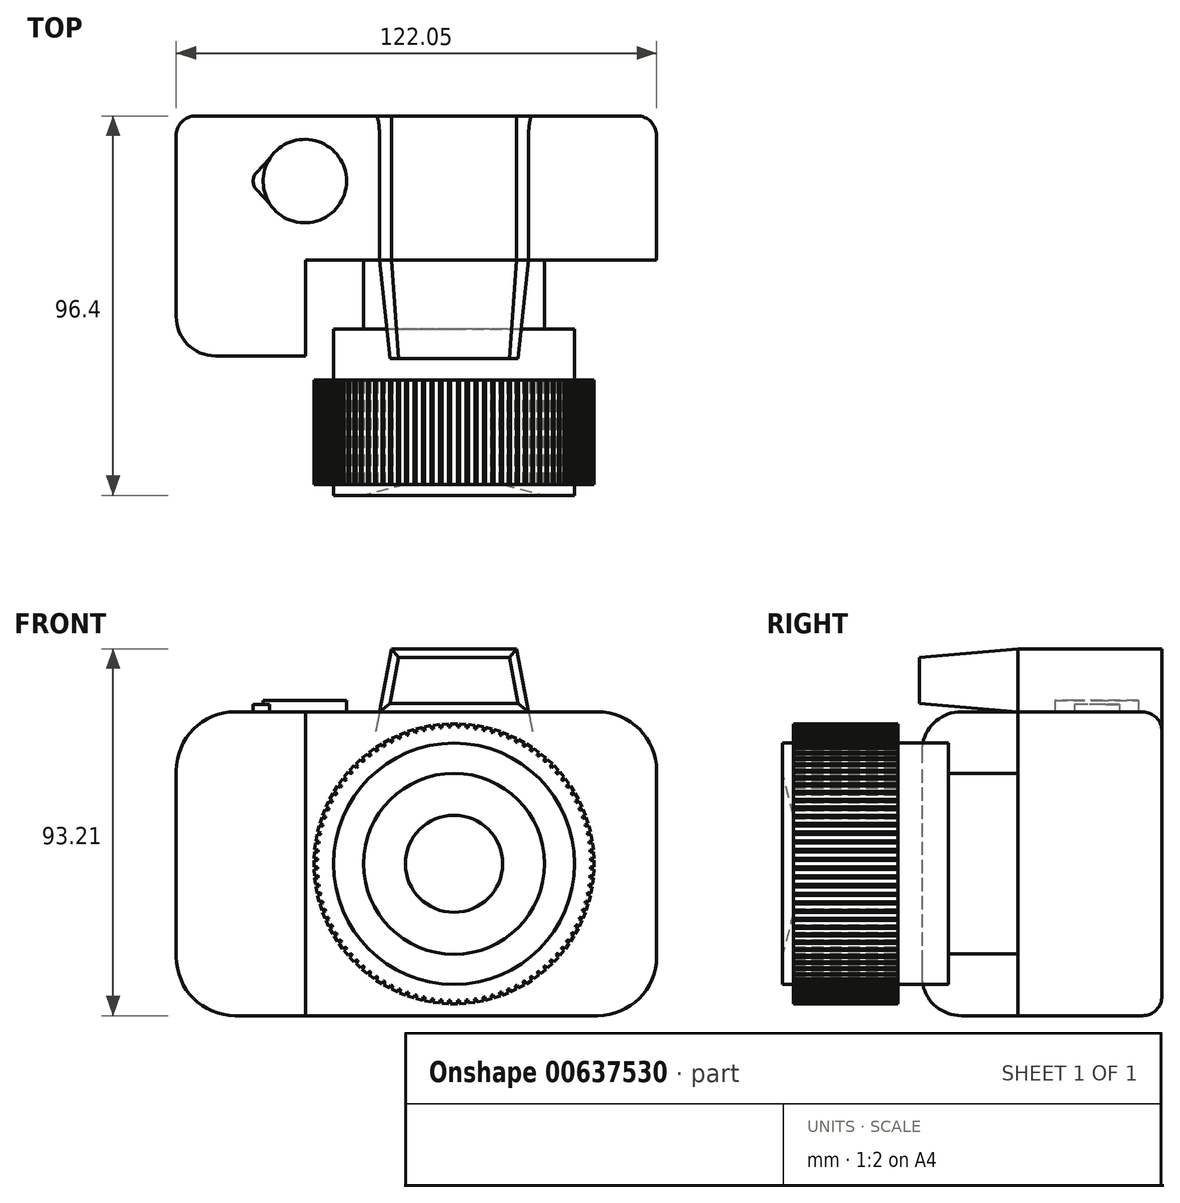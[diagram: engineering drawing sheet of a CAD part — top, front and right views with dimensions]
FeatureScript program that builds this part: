
annotation { "Feature Type Name" : "Feature", "Feature Type Description" : "" }
export const myFeature = defineFeature(function(context is Context, id is Id, definition is map)
    precondition{}
    {
        {
            var Q0;
            Q0=qCreatedBy(makeId("Front.planeOp"),FACE);
            var sketch = newSketch(context, id + "F0", { "sketchPlane" : qUnion([Q0])});
            skCircle(sketch, "E0", {"center": v(0, 0) * mm, "radius": 22.94 * mm});
            skCircle(sketch, "E1", {"center": v(0, 0) * mm, "radius": 26.37 * mm});
            skLineSegment(sketch, "E2", {"start": v(0, 54.62) * mm, "end": v(-15.9, 54.62) * mm});
            skLineSegment(sketch, "E3", {"start": v(-15.9, 54.62) * mm, "end": v(-24.34, 10.14) * mm});
            skLineSegment(sketch, "E4", {"start": v(-24.34, 10.14) * mm, "end": v(0, 10.14) * mm});
            skLineSegment(sketch, "E5.MirrorCS", {"start": v(0, 54.62) * mm, "end": v(15.9, 54.62) * mm});
            skLineSegment(sketch, "E6.MirrorCS", {"start": v(15.9, 54.62) * mm, "end": v(24.34, 10.14) * mm});
            skLineSegment(sketch, "E7.MirrorCS", {"start": v(24.34, 10.14) * mm, "end": v(0, 10.14) * mm});
            skCircle(sketch, "E8", {"center": v(0, 0) * mm, "radius": 34.73 * mm});
            skCircle(sketch, "E9", {"center": v(0, 0) * mm, "radius": 30.64 * mm});
            skSolve(sketch);
        }
        {
            var Q0;
            Q0=makeQuery(id+"F0.imprint","IMPRINT",FACE,{"disambiguationData":[TD([[makeQuery(id+"F0.imprint","IMPRINT",EDGE,{"derivedFrom":sQuery(id+"F0.wireOp",EDGE,"E0")}),1.0]])]});
            extrude(context, id + "F1", {"entities" : qUnion([Q0]), "depth" : 59.8 * mm, "offsetDistance" : 25 * mm});
        }
        {
            var Q0;
            Q0=makeQuery(id+"F0.imprint","IMPRINT",FACE,{"disambiguationData":[TD([[makeQuery(id+"F0.imprint","IMPRINT",EDGE,{"derivedFrom":sQuery(id+"F0.wireOp",EDGE,"E0")}),-1.0]])]});
            var Q1;
            {var subQ0=sQuery(id+"F0.wireOp",EDGE,"E3");var subQ5=sQuery(id+"F0.wireOp",EDGE,"E9");var subQ7=makeQuery(id+"F0.imprint","INTERSECT",VERTEX,{"derivedFrom":[subQ0,subQ5]});Q1=makeQuery(id+"F0.imprint","IMPRINT",FACE,{"disambiguationData":[TD([[makeQuery(id+"F0.imprint","IMPRINT",EDGE,{"disambiguationData":[TD([[subQ7,-1.0]])],"derivedFrom":subQ5}),1.0]])]});}
            var Q2;
            {var subQ0=sQuery(id+"F0.wireOp",EDGE,"E3");var subQ5=sQuery(id+"F0.wireOp",EDGE,"E9");var subQ6=makeQuery(id+"F0.imprint","INTERSECT",VERTEX,{"derivedFrom":[subQ0,subQ5]});Q2=makeQuery(id+"F0.imprint","IMPRINT",FACE,{"disambiguationData":[TD([[makeQuery(id+"F0.imprint","IMPRINT",EDGE,{"disambiguationData":[TD([[subQ6,1.0]])],"derivedFrom":subQ5}),1.0]])]});}
            var Q3;
            Q3=makeQuery(id+"F1.opExtrude","CAP_FACE",FACE,{"disambiguationData":[OSD([sQuery(id+"F0.wireOp",EDGE,"E0")])],"isStart":false});
            extrude(context, id + "F2", {"entities" : qUnion([Q0, Q1, Q2]), "operationType" : NewBodyOperationType.ADD, "endBound" : BoundingType.UP_TO_SURFACE, "depth" : 25 * mm, "endBoundEntityFace" : qUnion([Q3]), "offsetDistance" : 25 * mm, "hasSecondDirection" : true, "secondDirectionOppositeDirection" : false, "secondDirectionDepth" : 17.6 * mm});
        }
        {
            var Q0;
            Q0=qCreatedBy(makeId("Right.planeOp"),FACE);
            var sketch = newSketch(context, id + "F3", { "sketchPlane" : qUnion([Q0])});
            skLineSegment(sketch, "E10", {"start": v(-53.76, 0) * mm, "end": v(-60, -23.79) * mm});
            skLineSegment(sketch, "E11", {"start": v(-60, -23.79) * mm, "end": v(-60, 0) * mm});
            skLineSegment(sketch, "E12", {"start": v(-60, 0) * mm, "end": v(-53.76, 0) * mm});
            skSolve(sketch);
        }
        {
            var Q0;
            Q0=makeQuery(id+"F3.imprint","IMPRINT",FACE,{"disambiguationData":[TD([[makeQuery(id+"F3.imprint","IMPRINT",EDGE,{"derivedFrom":sQuery(id+"F3.wireOp",EDGE,"E10")}),-1.0]])]});
            var Q1;
            Q1=sQuery(id+"F3.wireOp",EDGE,"E12");
            revolve(context, id + "F4", {"operationType" : NewBodyOperationType.REMOVE, "entities" : qUnion([Q0]), "axis" : qUnion([Q1]), "revolveType" : RevolveType.FULL, "oppositeDirection" : true});
        }
        {
            var Q0;
            Q0=qCreatedBy(makeId("Front.planeOp"),FACE);
            var sketch = newSketch(context, id + "F5", { "sketchPlane" : qUnion([Q0])});
            skLineSegment(sketch, "E13.bottom", {"start": v(-55.59, 38.6) * mm, "end": v(36.46, 38.6) * mm});
            skPoint(sketch, "E14.visualSharp", {"position": v(51.46, 38.6) * mm});
            skArc(sketch, "E14.filletArc", {"start": v(51.46, 23.6) * mm, "mid": v(47.06, 34.2) * mm, "end": v(36.46, 38.6) * mm});
            skPoint(sketch, "E15.visualSharp", {"position": v(51.46, -43.73) * mm});
            skPoint(sketch, "E16.visualSharp", {"position": v(-70.59, 38.6) * mm});
            skArc(sketch, "E16.filletArc", {"start": v(-55.59, 38.6) * mm, "mid": v(-66.2, 34.2) * mm, "end": v(-70.59, 23.6) * mm});
            skPoint(sketch, "E17.visualSharp", {"position": v(-70.59, -43.73) * mm});
            skLineSegment(sketch, "E18.MirrorCS", {"start": v(-55.59, -38.6) * mm, "end": v(36.46, -38.6) * mm});
            skArc(sketch, "E19.MirrorCS", {"start": v(-55.59, -38.6) * mm, "mid": v(-66.2, -34.2) * mm, "end": v(-70.59, -23.6) * mm});
            skArc(sketch, "E20.MirrorCS", {"start": v(51.46, -23.6) * mm, "mid": v(47.06, -34.2) * mm, "end": v(36.46, -38.6) * mm});
            skLineSegment(sketch, "E21", {"start": v(51.46, 23.6) * mm, "end": v(51.46, -23.6) * mm});
            skLineSegment(sketch, "E22", {"start": v(-70.59, 23.6) * mm, "end": v(-70.59, -23.6) * mm});
            skLineSegment(sketch, "E23.0", {"start": v(-15.9, 54.62) * mm, "end": v(-24.34, 10.14) * mm});
            skLineSegment(sketch, "E24.0", {"start": v(15.9, 54.62) * mm, "end": v(24.34, 10.14) * mm});
            skLineSegment(sketch, "E25", {"start": v(18.94, 38.6) * mm, "end": v(-18.94, 38.6) * mm});
            skLineSegment(sketch, "E26", {"start": v(-18.94, 38.6) * mm, "end": v(-15.9, 54.62) * mm});
            skLineSegment(sketch, "E27", {"start": v(15.9, 54.62) * mm, "end": v(18.94, 38.6) * mm});
            skLineSegment(sketch, "E28", {"start": v(15.9, 54.62) * mm, "end": v(-15.9, 54.62) * mm});
            skSolve(sketch);
        }
        {
            var Q0;
            Q0=makeQuery(id+"F5.imprint","IMPRINT",FACE,{"disambiguationData":[TD([[makeQuery(id+"F5.imprint","IMPRINT",EDGE,{"derivedFrom":sQuery(id+"F5.wireOp",EDGE,"E13.bottom")}),-1.0]])]});
            var Q1;
            {var subQ4=sQuery(id+"F0.wireOp",EDGE,"E2");Q1=makeQuery(id+"F0.imprint","IMPRINT",FACE,{"disambiguationData":[TD([[makeQuery(id+"F0.imprint","IMPRINT",EDGE,{"derivedFrom":subQ4}),1.0]])]});}
            var Q2;
            {var subQ4=sQuery(id+"F0.wireOp",EDGE,"E5.MirrorCS");Q2=makeQuery(id+"F0.imprint","IMPRINT",FACE,{"disambiguationData":[TD([[makeQuery(id+"F0.imprint","IMPRINT",EDGE,{"derivedFrom":subQ4}),-1.0]])]});}
            extrude(context, id + "F6", {"entities" : qUnion([Q0, Q1, Q2]), "operationType" : NewBodyOperationType.ADD, "oppositeDirection" : true, "depth" : 36.6 * mm, "offsetDistance" : 25 * mm});
        }
        {
            var Q0;
            Q0=qCreatedBy(makeId("Front.planeOp"),FACE);
            var sketch = newSketch(context, id + "F7", { "sketchPlane" : qUnion([Q0])});
            skLineSegment(sketch, "E29.0", {"start": v(0, 54.62) * mm, "end": v(-15.9, 54.62) * mm});
            skLineSegment(sketch, "E30.0", {"start": v(0, 54.62) * mm, "end": v(15.9, 54.62) * mm});
            skLineSegment(sketch, "E31.0", {"start": v(-15.9, 54.62) * mm, "end": v(-24.34, 10.14) * mm});
            skLineSegment(sketch, "E32.0", {"start": v(15.9, 54.62) * mm, "end": v(24.34, 10.14) * mm});
            skLineSegment(sketch, "E33.0", {"start": v(-55.59, 38.6) * mm, "end": v(-18.94, 38.6) * mm});
            skLineSegment(sketch, "E34", {"start": v(-18.94, 38.6) * mm, "end": v(18.94, 38.6) * mm});
            skLineSegment(sketch, "E35", {"start": v(18.94, 38.6) * mm, "end": v(15.9, 54.62) * mm});
            skLineSegment(sketch, "E36", {"start": v(-15.9, 54.62) * mm, "end": v(15.9, 54.62) * mm});
            skSolve(sketch);
        }
        {
            var Q0;
            {var subQ2=sQuery(id+"F7.wireOp",EDGE,"E34");Q0=makeQuery(id+"F7.imprint","IMPRINT",FACE,{"disambiguationData":[TD([[makeQuery(id+"F7.imprint","IMPRINT",EDGE,{"derivedFrom":subQ2}),1.0]])]});}
            extrude(context, id + "F8", {"entities" : qUnion([Q0]), "operationType" : NewBodyOperationType.ADD, "depth" : 25 * mm, "offsetDistance" : 25 * mm, "hasDraft" : true, "draftAngle" : 5 * degree, "draftPullDirection" : true});
        }
        {
            var Q0;
            Q0=qCreatedBy(makeId("Top.planeOp"),FACE);
            var sketch = newSketch(context, id + "F9", { "sketchPlane" : qUnion([Q0])});
            skLineSegment(sketch, "E37.0", {"start": v(-55.59, 0) * mm, "end": v(-70.59, 0) * mm});
            skLineSegment(sketch, "E38", {"start": v(-70.59, 0) * mm, "end": v(-37.71, 0) * mm});
            skLineSegment(sketch, "E39", {"start": v(-37.71, 0) * mm, "end": v(-37.71, -24.4) * mm});
            skLineSegment(sketch, "E40", {"start": v(-37.71, -24.4) * mm, "end": v(-70.59, -24.4) * mm});
            skLineSegment(sketch, "E41", {"start": v(-70.59, -24.4) * mm, "end": v(-70.59, 0) * mm});
            skSolve(sketch);
        }
        {
            var Q0;
            {var subQ2=sQuery(id+"F9.wireOp",EDGE,"E39");Q0=makeQuery(id+"F9.imprint","IMPRINT",FACE,{"disambiguationData":[TD([[makeQuery(id+"F9.imprint","IMPRINT",EDGE,{"derivedFrom":subQ2}),-1.0]])]});}
            var Q1;
            {var subQ0=sQuery(id+"F0.wireOp",EDGE,"E3");var subQ5=sQuery(id+"F5.wireOp",EDGE,"E25");var subQ13=sQuery(id+"F5.wireOp",EDGE,"E13.bottom");Q1=makeQuery(id+"F6.boolean.opBoolean","SPLIT",FACE,{"disambiguationData":[TD([makeQuery(id+"F6.opExtrude","SWEPT_FACE",FACE,{"disambiguationData":[OSD([subQ0])]})])],"derivedFrom":makeQuery(id+"F6.opExtrude","SWEPT_FACE",FACE,{"disambiguationData":[OSD([subQ13,subQ5])]})});}
            var Q2;
            Q2=makeQuery(id+"F6.opExtrude","SWEPT_FACE",FACE,{"disambiguationData":[OSD([sQuery(id+"F5.wireOp",EDGE,"E18.MirrorCS")])]});
            extrude(context, id + "F10", {"entities" : qUnion([Q0]), "operationType" : NewBodyOperationType.ADD, "endBound" : BoundingType.UP_TO_SURFACE, "depth" : 25 * mm, "endBoundEntityFace" : qUnion([Q1]), "offsetDistance" : 25 * mm, "hasSecondDirection" : true, "secondDirectionBound" : SecondDirectionBoundingType.UP_TO_SURFACE, "secondDirectionOppositeDirection" : true, "secondDirectionDepth" : 25 * mm, "secondDirectionBoundEntityFace" : qUnion([Q2])});
        }
        {
            var Q0;
            Q0=makeQuery(id+"F10.opExtrude","CAP_EDGE",EDGE,{"disambiguationData":[OSD([sQuery(id+"F9.wireOp",EDGE,"E41")])],"isStart":false});
            var Q1;
            Q1=makeQuery(id+"F10.opExtrude","CAP_EDGE",EDGE,{"disambiguationData":[OSD([sQuery(id+"F9.wireOp",EDGE,"E41")])],"isStart":true});
            fillet(context, id + "F11", {"entities" : qUnion([Q0, Q1]), "radius" : 15 * mm, "tangentPropagation" : true, "allowEdgeOverflow" : false});
        }
        {
            var Q0;
            Q0=makeQuery(id+"F10.opExtrude","TWEAK_EDGE",EDGE,{"derivedFrom":[makeQuery(id+"F9.imprint","IMPRINT",EDGE,{"derivedFrom":sQuery(id+"F9.wireOp",EDGE,"E39")}),makeQuery(id+"F9.imprint","IMPRINT",EDGE,{"derivedFrom":sQuery(id+"F9.wireOp",EDGE,"E40")})]});
            var Q1;
            Q1=makeQuery(id+"F10.opExtrude","CAP_EDGE",EDGE,{"disambiguationData":[OSD([sQuery(id+"F9.wireOp",EDGE,"E40")])],"isStart":false});
            fillet(context, id + "F12", {"entities" : qUnion([Q0, Q1]), "radius" : 10 * mm, "tangentPropagation" : true, "allowEdgeOverflow" : false});
        }
        {
            var Q0;
            {var subQ0=sQuery(id+"F0.wireOp",EDGE,"E3");var subQ1=sQuery(id+"F5.wireOp",EDGE,"E25");var subQ9=sQuery(id+"F5.wireOp",EDGE,"E13.bottom");Q0=makeQuery(id+"F10.boolean.opBoolean","MERGE",FACE,{"derivedFrom":[makeQuery(id+"F6.boolean.opBoolean","SPLIT",FACE,{"disambiguationData":[TD([makeQuery(id+"F6.opExtrude","SWEPT_FACE",FACE,{"disambiguationData":[OSD([subQ0])]})])],"derivedFrom":makeQuery(id+"F6.opExtrude","SWEPT_FACE",FACE,{"disambiguationData":[OSD([subQ9,subQ1])]})}),makeQuery(id+"F10.opExtrude","CAP_FACE",FACE,{"disambiguationData":[OSD([sQuery(id+"F9.wireOp",EDGE,"E38"),sQuery(id+"F9.wireOp",EDGE,"E39"),sQuery(id+"F9.wireOp",EDGE,"E40"),sQuery(id+"F9.wireOp",EDGE,"E41")])],"isStart":false})]});}
            var sketch = newSketch(context, id + "F13", { "sketchPlane" : qUnion([Q0])});
            skCircle(sketch, "E42", {"center": v(-37.91, 20.04) * mm, "radius": 10.6 * mm});
            skLineSegment(sketch, "E43", {"start": v(-52.33, 20.04) * mm, "end": v(-46.82, 25.77) * mm});
            skLineSegment(sketch, "E44", {"start": v(-52.33, 20.04) * mm, "end": v(-37.91, 20.04) * mm});
            skLineSegment(sketch, "E45.MirrorCS", {"start": v(-52.33, 20.04) * mm, "end": v(-46.82, 14.3) * mm});
            skSolve(sketch);
        }
        {
            var Q0;
            Q0=makeQuery(id+"F13.imprint","IMPRINT",FACE,{"disambiguationData":[TD([[makeQuery(id+"F13.imprint","IMPRINT",EDGE,{"derivedFrom":sQuery(id+"F13.wireOp",EDGE,"E42")}),1.0]])]});
            extrude(context, id + "F14", {"entities" : qUnion([Q0]), "operationType" : NewBodyOperationType.ADD, "depth" : 2.9 * mm, "offsetDistance" : 25 * mm});
        }
        {
            var Q0;
            {var subQ0=sQuery(id+"F0.wireOp",EDGE,"E3");var subQ5=sQuery(id+"F0.wireOp",EDGE,"E8");var subQ6=makeQuery(id+"F0.imprint","INTERSECT",VERTEX,{"derivedFrom":[subQ0,subQ5]});Q0=makeQuery(id+"F0.imprint","IMPRINT",FACE,{"disambiguationData":[TD([[makeQuery(id+"F0.imprint","IMPRINT",EDGE,{"disambiguationData":[TD([[subQ6,-1.0]])],"derivedFrom":subQ5}),1.0]])]});}
            var Q1;
            {var subQ0=sQuery(id+"F0.wireOp",EDGE,"E3");var subQ5=sQuery(id+"F0.wireOp",EDGE,"E8");var subQ6=makeQuery(id+"F0.imprint","INTERSECT",VERTEX,{"derivedFrom":[subQ0,subQ5]});Q1=makeQuery(id+"F0.imprint","IMPRINT",FACE,{"disambiguationData":[TD([[makeQuery(id+"F0.imprint","IMPRINT",EDGE,{"disambiguationData":[TD([[subQ6,1.0]])],"derivedFrom":subQ5}),1.0]])]});}
            var Q2;
            {var subQ0=sQuery(id+"F0.wireOp",EDGE,"E0");Q2=makeQuery(id+"F2.boolean.opBoolean","MERGE",FACE,{"derivedFrom":[makeQuery(id+"F1.opExtrude","CAP_FACE",FACE,{"disambiguationData":[OSD([subQ0])],"isStart":false}),makeQuery(id+"F2.opExtrude","CAP_FACE",FACE,{"disambiguationData":[OSD([subQ0,sQuery(id+"F0.wireOp",EDGE,"E9")])],"isStart":false})]});}
            extrude(context, id + "F15", {"entities" : qUnion([Q0, Q1]), "operationType" : NewBodyOperationType.ADD, "depth" : 57 * mm, "endBoundEntityFace" : qUnion([Q2]), "offsetDistance" : 25 * mm, "hasSecondDirection" : true, "secondDirectionOppositeDirection" : false, "secondDirectionDepth" : 30.5 * mm});
        }
        {
            var Q0;
            {var subQ0=sQuery(id+"F13.wireOp",EDGE,"E43");Q0=makeQuery(id+"F13.imprint","IMPRINT",FACE,{"disambiguationData":[TD([[makeQuery(id+"F13.imprint","IMPRINT",EDGE,{"derivedFrom":subQ0}),-1.0]])]});}
            var Q1;
            {var subQ0=sQuery(id+"F13.wireOp",EDGE,"E45.MirrorCS");Q1=makeQuery(id+"F13.imprint","IMPRINT",FACE,{"disambiguationData":[TD([[makeQuery(id+"F13.imprint","IMPRINT",EDGE,{"derivedFrom":subQ0}),1.0]])]});}
            extrude(context, id + "F16", {"entities" : qUnion([Q0, Q1]), "operationType" : NewBodyOperationType.ADD, "depth" : 1.83 * mm, "offsetDistance" : 25 * mm});
        }
        {
            var Q0;
            Q0=makeQuery(id+"F16.opExtrude","SWEPT_EDGE",EDGE,{"disambiguationData":[OSD([sQuery(id+"F13.wireOp",EDGE,"E43"),sQuery(id+"F13.wireOp",EDGE,"E44"),sQuery(id+"F13.wireOp",EDGE,"E45.MirrorCS")])]});
            fillet(context, id + "F17", {"entities" : qUnion([Q0]), "radius" : 3.36 * mm, "tangentPropagation" : true, "allowEdgeOverflow" : false});
        }
        {
            var Q0;
            Q0=makeQuery(id+"F6.opExtrude","CAP_EDGE",EDGE,{"disambiguationData":[OSD([sQuery(id+"F5.wireOp",EDGE,"E21")])],"isStart":false});
            fillet(context, id + "F18", {"entities" : qUnion([Q0]), "radius" : 5 * mm, "tangentPropagation" : true, "allowEdgeOverflow" : false});
        }
        {
            var Q0;
            Q0=qCreatedBy(makeId("Front.planeOp"),FACE);
            var sketch = newSketch(context, id + "F19", { "sketchPlane" : qUnion([Q0])});
            skLineSegment(sketch, "E46.bottom", {"start": v(-0.83, 0) * mm, "end": v(0.83, 0) * mm});
            skLineSegment(sketch, "E46.top", {"start": v(-0.83, 35.56) * mm, "end": v(0.83, 35.56) * mm});
            skLineSegment(sketch, "E46.left", {"start": v(-0.83, 0) * mm, "end": v(-0.83, 35.56) * mm});
            skLineSegment(sketch, "E46.right", {"start": v(0.83, 0) * mm, "end": v(0.83, 35.56) * mm});
            skSolve(sketch);
        }
        {
            var Q0;
            Q0=makeQuery(id+"F19.imprint","IMPRINT",FACE,{"disambiguationData":[TD([[makeQuery(id+"F19.imprint","IMPRINT",EDGE,{"derivedFrom":sQuery(id+"F19.wireOp",EDGE,"E46.bottom")}),1.0]])]});
            var Q1;
            Q1=makeQuery(id+"F15.opExtrude","CAP_FACE",FACE,{"disambiguationData":[OSD([sQuery(id+"F0.wireOp",EDGE,"E1"),sQuery(id+"F0.wireOp",EDGE,"E8")])],"isStart":false});
            var Q2;
            Q2=makeQuery(id+"F15.opExtrude","CAP_FACE",FACE,{"disambiguationData":[OSD([sQuery(id+"F0.wireOp",EDGE,"E1"),sQuery(id+"F0.wireOp",EDGE,"E8")])],"isStart":true});
            extrude(context, id + "F20", {"entities" : qUnion([Q0]), "endBound" : BoundingType.UP_TO_SURFACE, "depth" : 25 * mm, "endBoundEntityFace" : qUnion([Q1]), "offsetDistance" : 25 * mm, "hasSecondDirection" : true, "secondDirectionBound" : SecondDirectionBoundingType.UP_TO_SURFACE, "secondDirectionOppositeDirection" : false, "secondDirectionDepth" : 25 * mm, "secondDirectionBoundEntityFace" : qUnion([Q2])});
        }
        {
            var Q0;
            Q0=makeQuery(id+"F20.opExtrude","SWEPT_BODY",BODY,{"disambiguationData":[OSD([sQuery(id+"F19.wireOp",EDGE,"E46.bottom"),sQuery(id+"F19.wireOp",EDGE,"E46.top"),sQuery(id+"F19.wireOp",EDGE,"E46.left"),sQuery(id+"F19.wireOp",EDGE,"E46.right")])]});
            var Q1;
            Q1=makeQuery(id+"F4.boolean.opBoolean","COPY",FACE,{"derivedFrom":makeQuery(id+"F4.opRevolve","SWEPT_FACE",FACE,{"disambiguationData":[OSD([sQuery(id+"F3.wireOp",EDGE,"E10")])]})});
            circularPattern(context, id + "F21", {"operationType" : NewBodyOperationType.ADD, "entities" : qUnion([Q0]), "axis" : qUnion([Q1]), "angle" : 360 * degree, "instanceCount" : 100, "equalSpace" : true, "isCentered" : true});
        }
    });
